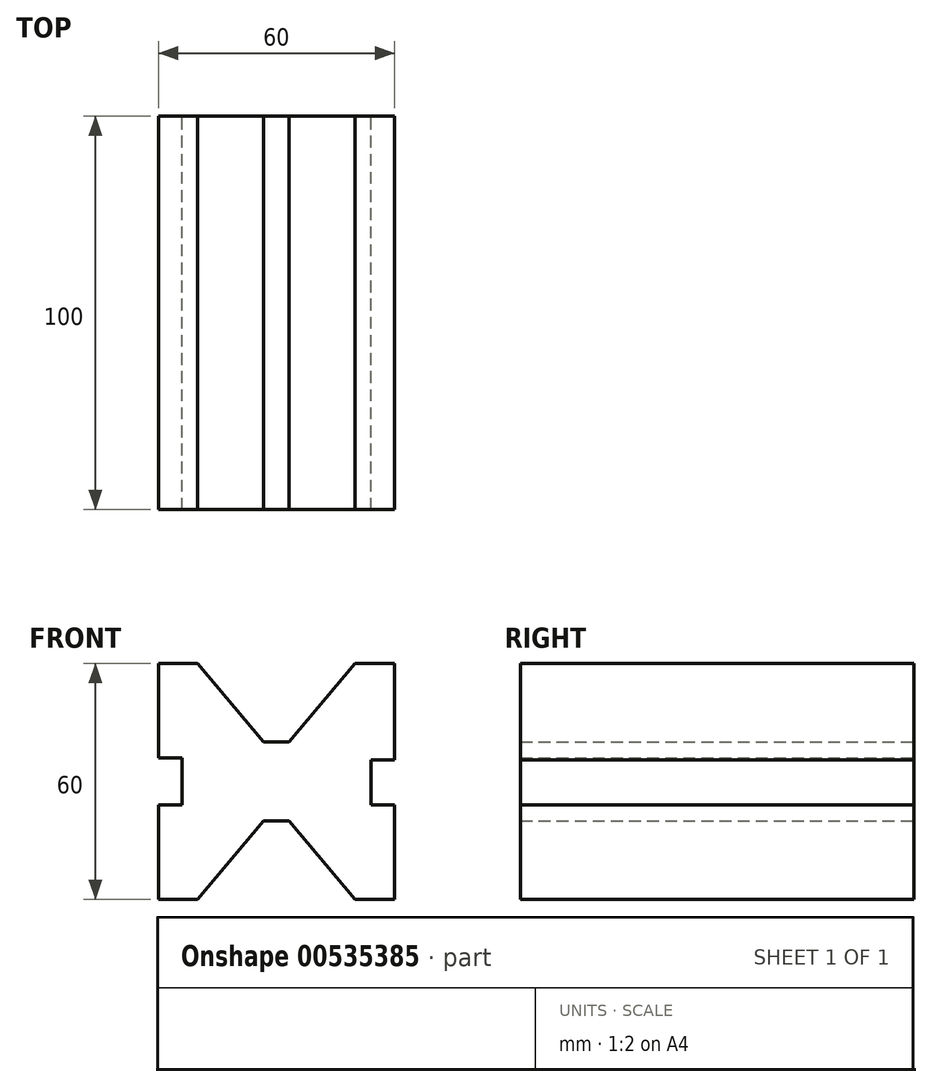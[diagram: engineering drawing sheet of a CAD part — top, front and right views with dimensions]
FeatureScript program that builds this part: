
annotation { "Feature Type Name" : "Feature", "Feature Type Description" : "" }
export const myFeature = defineFeature(function(context is Context, id is Id, definition is map)
    precondition{}
    {
        {
            var Q0;
            Q0=qCreatedBy(makeId("Front.planeOp"),FACE);
            var sketch = newSketch(context, id + "F0", { "sketchPlane" : qUnion([Q0])});
            skLineSegment(sketch, "E0.bottom", {"start": v(-22.23, 24) * mm, "end": v(-12.23, 24) * mm});
            skLineSegment(sketch, "E0.left", {"start": v(-22.23, 24) * mm, "end": v(-22.23, 0) * mm});
            skLineSegment(sketch, "E1", {"start": v(-12.23, 24) * mm, "end": v(4.55, 4) * mm});
            skLineSegment(sketch, "E2", {"start": v(-22.23, 0) * mm, "end": v(-16.23, 0) * mm});
            skLineSegment(sketch, "E3.MirrorCS", {"start": v(37.77, -0.53) * mm, "end": v(31.77, -0.53) * mm});
            skLineSegment(sketch, "E4.MirrorCS", {"start": v(37.77, 24) * mm, "end": v(37.77, -0.53) * mm});
            skLineSegment(sketch, "E5.MirrorCS", {"start": v(27.77, 24) * mm, "end": v(10.99, 4) * mm});
            skLineSegment(sketch, "E6.MirrorCS", {"start": v(37.77, 24) * mm, "end": v(27.77, 24) * mm});
            skLineSegment(sketch, "E7.MirrorCS", {"start": v(37.77, -36) * mm, "end": v(27.77, -36) * mm});
            skLineSegment(sketch, "E8.MirrorCS", {"start": v(27.77, -36) * mm, "end": v(10.99, -16) * mm});
            skLineSegment(sketch, "E9.MirrorCS", {"start": v(37.77, -36) * mm, "end": v(37.77, -12) * mm});
            skLineSegment(sketch, "E10.MirrorCS", {"start": v(-22.23, -36) * mm, "end": v(-12.23, -36) * mm});
            skLineSegment(sketch, "E11.MirrorCS", {"start": v(37.77, -12) * mm, "end": v(31.77, -12) * mm});
            skLineSegment(sketch, "E12.MirrorCS", {"start": v(-12.23, -36) * mm, "end": v(4.55, -16) * mm});
            skLineSegment(sketch, "E13.MirrorCS", {"start": v(-22.23, -36) * mm, "end": v(-22.23, -12) * mm});
            skLineSegment(sketch, "E14.MirrorCS", {"start": v(-22.23, -12) * mm, "end": v(-16.23, -12) * mm});
            skPoint(sketch, "E15.MirrorCS.end.orphan", {"position": v(7.77, -5.74) * mm});
            skLineSegment(sketch, "E16", {"start": v(4.55, 4) * mm, "end": v(10.99, 4) * mm});
            skLineSegment(sketch, "E17", {"start": v(31.77, -12) * mm, "end": v(31.77, -0.53) * mm});
            skLineSegment(sketch, "E18", {"start": v(10.99, -16) * mm, "end": v(4.55, -16) * mm});
            skLineSegment(sketch, "E19", {"start": v(-16.23, -12) * mm, "end": v(-16.23, 0) * mm});
            skSolve(sketch);
        }
        {
            var Q0;
            Q0 = qSketchRegion(id + "F0", true);
            extrude(context, id + "F1", {"entities" : qUnion([Q0]), "depth" : 100 * mm, "offsetDistance" : 25 * mm});
        }
    });
